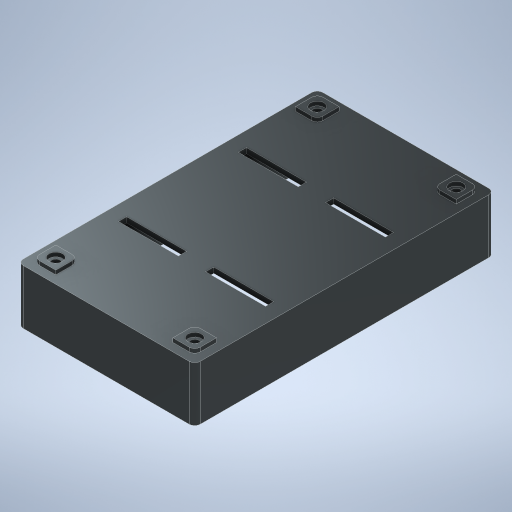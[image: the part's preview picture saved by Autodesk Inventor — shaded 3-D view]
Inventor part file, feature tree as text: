
AUTODESK INVENTOR PART (.ipt)
format: ipt  version: 2023 (Build 270158000, 158)  size: 422,912 bytes
history: native  units: in
note: dims shown in document units (in); Inventor stores cm internally (conversion verified against a paired STEP export)
features: extrude x8, sketch x5
ambient origin geometry x8: Origin, YZ Plane, XZ Plane, XY Plane, X Axis, Y Axis, Z Axis, Center Point
bodies: Body1 (feature_tree)
feature tree (13):
  sketch  "Sketch1"  dims[d0=4.3307in d1=2.5591in]
  extrude  "Extrusion18"  Depth=2.5591in
  extrude  "Extrusion19"  Depth=0.1181in
  extrude  "Extrusion20"  Depth=0.0787in
  extrude  "Extrusion21"  Depth=0.7087in TaperAngle=0.0deg
  extrude  "Extrusion22"  Depth=0.8465in TaperAngle=0.0deg
  extrude  "Extrusion23"  Depth=0.1969in
  extrude  "Extrusion24"  Depth=0.1969in
  extrude  "Extrusion25"  Depth=0.1969in
  sketch  "Sketch11"  dims[d2=0.1181in d4=0.1181in]
  sketch  "Sketch12"  dims[d5=0.1181in d8=0.0787in]
  sketch  "Sketch13"  dims[d158=0.7874in d159=0.0in d160=0.7087in d161=0.0in]
  sketch  "Sketch14"  dims[d162=0.7874in d163=0.0in d164=0.8465in d165=0.0in d166=0.1969in d167=0.1969in d168=0.1969in d169=0.1969in d170=0.0591in d171=0.0in d173=1.063in d174=1.063in d179=0.315in d180=0.0984in d181=0.0394in d182=0.0394in d183=0.1181in d184=0.0in d189=0.1181in d190=0.0in d194=0.3937in d195=0.7874in d196=0.0394in d197=0.1181in d198=0.0in d202=0.8661in d203=0.1181in d58=0.0197in d59=0.0344in d60=0.0197in d61=0.0344in d106=0.0197in d107=0.0344in d108=0.0197in d109=0.0344in d124=0.0197in d125=0.0344in d126=0.0197in d127=0.0344in d128=0.0197in d129=0.0344in d136=0.0197in d137=0.0344in d138=0.0197in d139=0.0344in d144=0.0197in d145=0.0344in d146=0.0197in d147=0.0344in]
